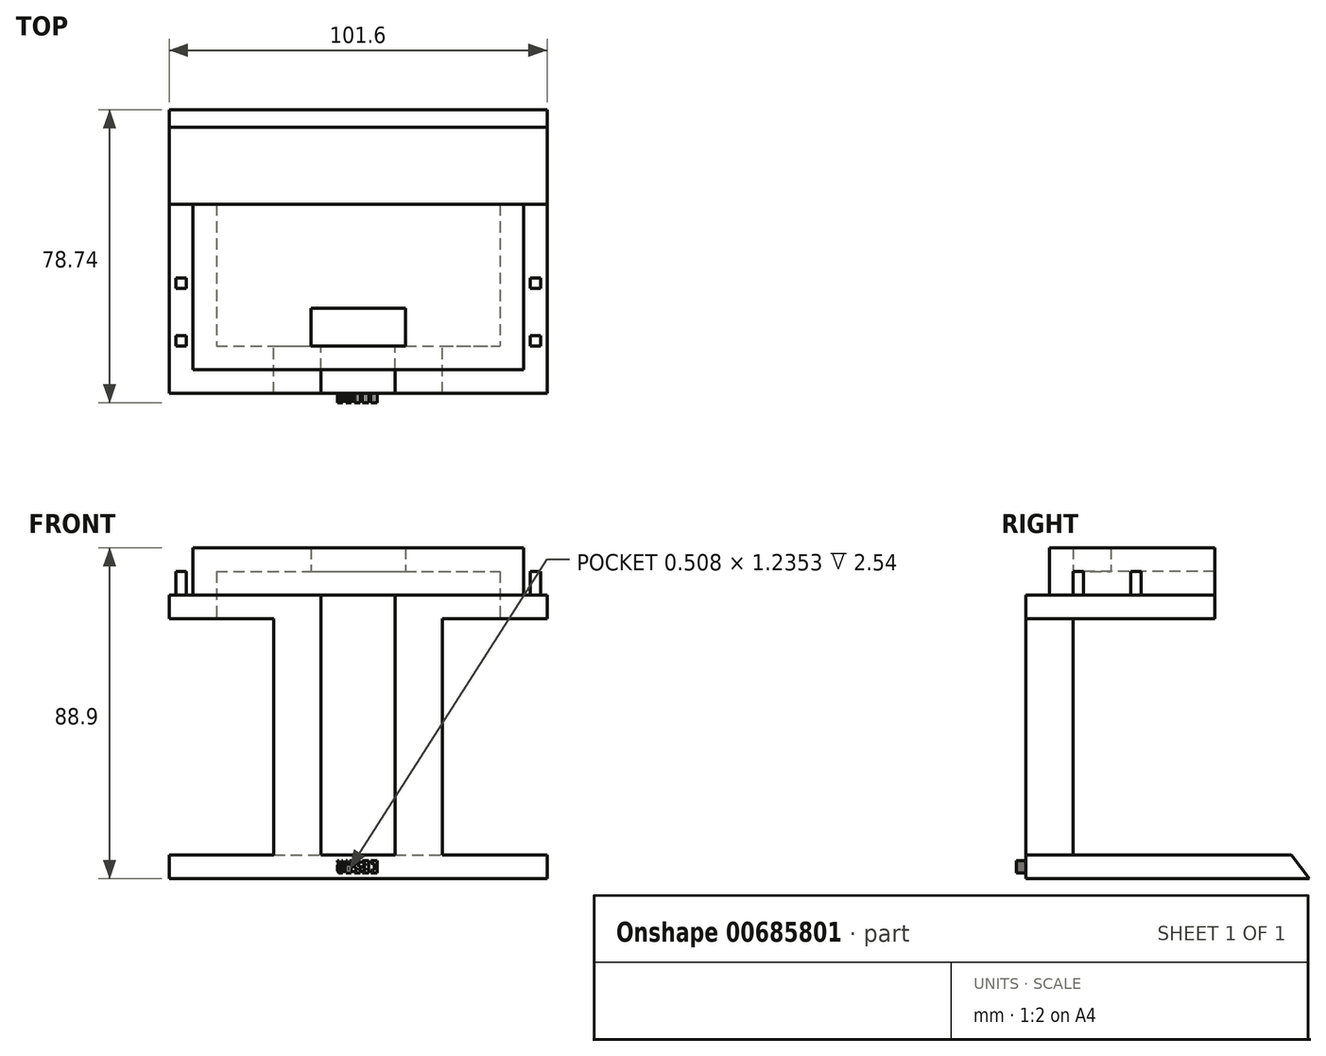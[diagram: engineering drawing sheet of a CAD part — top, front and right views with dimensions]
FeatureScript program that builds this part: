
annotation { "Feature Type Name" : "Feature", "Feature Type Description" : "" }
export const myFeature = defineFeature(function(context is Context, id is Id, definition is map)
    precondition{}
    {
        {
            var Q0;
            Q0=qCreatedBy(makeId("Top.planeOp"),FACE);
            var sketch = newSketch(context, id + "F0", { "sketchPlane" : qUnion([Q0])});
            skLineSegment(sketch, "E0.bottom", {"start": v(-43.67, 17.4) * mm, "end": v(57.93, 17.4) * mm});
            skLineSegment(sketch, "E0.top", {"start": v(-43.67, -33.4) * mm, "end": v(57.93, -33.4) * mm});
            skLineSegment(sketch, "E0.left", {"start": v(-43.67, 17.4) * mm, "end": v(-43.67, -33.4) * mm});
            skLineSegment(sketch, "E0.right", {"start": v(57.93, 17.4) * mm, "end": v(57.93, -33.4) * mm});
            skSolve(sketch);
        }
        {
            var Q0;
            Q0=makeQuery(id+"F0.imprint","IMPRINT",FACE,{"disambiguationData":[TD([[makeQuery(id+"F0.imprint","IMPRINT",EDGE,{"derivedFrom":sQuery(id+"F0.wireOp",EDGE,"E0.bottom")}),-1.0]])]});
            extrude(context, id + "F1", {"entities" : qUnion([Q0]), "depth" : 19.05 * mm, "offsetDistance" : 25.4 * mm});
        }
        {
            var Q0;
            Q0=makeQuery(id+"F1.opExtrude","CAP_FACE",FACE,{"disambiguationData":[OSD([sQuery(id+"F0.wireOp",EDGE,"E0.bottom"),sQuery(id+"F0.wireOp",EDGE,"E0.top"),sQuery(id+"F0.wireOp",EDGE,"E0.left"),sQuery(id+"F0.wireOp",EDGE,"E0.right")])],"isStart":false});
            var sketch = newSketch(context, id + "F2", { "sketchPlane" : qUnion([Q0])});
            skLineSegment(sketch, "E1.bottom", {"start": v(-37.32, 17.4) * mm, "end": v(51.58, 17.4) * mm});
            skLineSegment(sketch, "E1.top", {"start": v(-37.32, -33.4) * mm, "end": v(51.58, -33.4) * mm});
            skLineSegment(sketch, "E1.left", {"start": v(-37.32, 17.4) * mm, "end": v(-37.32, -33.4) * mm});
            skLineSegment(sketch, "E1.right", {"start": v(51.58, 17.4) * mm, "end": v(51.58, -33.4) * mm});
            skLineSegment(sketch, "E2", {"start": v(-37.32, -27.04) * mm, "end": v(51.58, -27.04) * mm});
            skSolve(sketch);
        }
        {
            var Q0;
            {var subQ0=makeQuery(id+"F1.opExtrude","CAP_EDGE",EDGE,{"disambiguationData":[OSD([sQuery(id+"F0.wireOp",EDGE,"E0.left")])],"isStart":false});Q0=makeQuery(id+"F2.imprint","IMPRINT",FACE,{"disambiguationData":[TD([[makeQuery(id+"F2.imprint","IMPRINT",EDGE,{"derivedFrom":subQ0}),1.0]])]});}
            var Q1;
            {var subQ0=sQuery(id+"F2.wireOp",EDGE,"E1.top");Q1=makeQuery(id+"F2.imprint","IMPRINT",FACE,{"disambiguationData":[TD([[makeQuery(id+"F2.imprint","IMPRINT",EDGE,{"derivedFrom":subQ0}),1.0]])]});}
            var Q2;
            {var subQ0=makeQuery(id+"F1.opExtrude","CAP_EDGE",EDGE,{"disambiguationData":[OSD([sQuery(id+"F0.wireOp",EDGE,"E0.right")])],"isStart":false});Q2=makeQuery(id+"F2.imprint","IMPRINT",FACE,{"disambiguationData":[TD([[makeQuery(id+"F2.imprint","IMPRINT",EDGE,{"derivedFrom":subQ0}),-1.0]])]});}
            extrude(context, id + "F3", {"entities" : qUnion([Q0, Q1, Q2]), "operationType" : NewBodyOperationType.REMOVE, "oppositeDirection" : true, "depth" : 12.7 * mm, "offsetDistance" : 25.4 * mm});
        }
        {
            var Q0;
            Q0=makeQuery(id+"F1.opExtrude","CAP_FACE",FACE,{"disambiguationData":[OSD([sQuery(id+"F0.wireOp",EDGE,"E0.bottom"),sQuery(id+"F0.wireOp",EDGE,"E0.top"),sQuery(id+"F0.wireOp",EDGE,"E0.left"),sQuery(id+"F0.wireOp",EDGE,"E0.right")])],"isStart":true});
            var sketch = newSketch(context, id + "F4", { "sketchPlane" : qUnion([Q0])});
            skLineSegment(sketch, "E3.bottom", {"start": v(-30.97, -17.4) * mm, "end": v(45.23, -17.4) * mm});
            skLineSegment(sketch, "E3.top", {"start": v(-30.97, 20.7) * mm, "end": v(45.23, 20.7) * mm});
            skLineSegment(sketch, "E3.left", {"start": v(-30.97, -17.4) * mm, "end": v(-30.97, 20.7) * mm});
            skLineSegment(sketch, "E3.right", {"start": v(45.23, -17.4) * mm, "end": v(45.23, 20.7) * mm});
            skSolve(sketch);
        }
        {
            var Q0;
            Q0=makeQuery(id+"F4.imprint","IMPRINT",FACE,{"disambiguationData":[TD([[makeQuery(id+"F4.imprint","IMPRINT",EDGE,{"derivedFrom":sQuery(id+"F4.wireOp",EDGE,"E3.bottom")}),1.0]])]});
            extrude(context, id + "F5", {"entities" : qUnion([Q0]), "operationType" : NewBodyOperationType.REMOVE, "oppositeDirection" : true, "depth" : 12.7 * mm, "offsetDistance" : 25.4 * mm});
        }
        {
            var Q0;
            Q0=makeQuery(id+"F5.boolean.opBoolean","COPY",FACE,{"derivedFrom":makeQuery(id+"F5.opExtrude","CAP_FACE",FACE,{"disambiguationData":[OSD([sQuery(id+"F4.wireOp",EDGE,"E3.bottom"),sQuery(id+"F4.wireOp",EDGE,"E3.top"),sQuery(id+"F4.wireOp",EDGE,"E3.left"),sQuery(id+"F4.wireOp",EDGE,"E3.right")])],"isStart":false})});
            var sketch = newSketch(context, id + "F6", { "sketchPlane" : qUnion([Q0])});
            skLineSegment(sketch, "E4.bottom", {"start": v(-5.57, 20.7) * mm, "end": v(19.83, 20.7) * mm});
            skLineSegment(sketch, "E4.top", {"start": v(-5.57, 10.53) * mm, "end": v(19.83, 10.53) * mm});
            skLineSegment(sketch, "E4.left", {"start": v(-5.57, 20.7) * mm, "end": v(-5.57, 10.53) * mm});
            skLineSegment(sketch, "E4.right", {"start": v(19.83, 20.7) * mm, "end": v(19.83, 10.53) * mm});
            skSolve(sketch);
        }
        {
            var Q0;
            Q0=makeQuery(id+"F6.imprint","IMPRINT",FACE,{"disambiguationData":[TD([[makeQuery(id+"F6.imprint","IMPRINT",EDGE,{"derivedFrom":sQuery(id+"F6.wireOp",EDGE,"E4.bottom")}),-1.0]])]});
            extrude(context, id + "F7", {"entities" : qUnion([Q0]), "operationType" : NewBodyOperationType.REMOVE, "oppositeDirection" : true, "depth" : 25.4 * mm, "offsetDistance" : 25.4 * mm});
        }
        {
            var Q0;
            Q0=makeQuery(id+"F1.opExtrude","CAP_FACE",FACE,{"disambiguationData":[OSD([sQuery(id+"F0.wireOp",EDGE,"E0.bottom"),sQuery(id+"F0.wireOp",EDGE,"E0.top"),sQuery(id+"F0.wireOp",EDGE,"E0.left"),sQuery(id+"F0.wireOp",EDGE,"E0.right")])],"isStart":true});
            var sketch = newSketch(context, id + "F8", { "sketchPlane" : qUnion([Q0])});
            skLineSegment(sketch, "E5.bottom", {"start": v(-2.83, 33.4) * mm, "end": v(17.08, 33.4) * mm});
            skLineSegment(sketch, "E5.top", {"start": v(-2.83, 20.7) * mm, "end": v(17.08, 20.7) * mm});
            skLineSegment(sketch, "E5.left", {"start": v(-2.83, 33.4) * mm, "end": v(-2.83, 20.7) * mm});
            skLineSegment(sketch, "E5.right", {"start": v(17.08, 33.4) * mm, "end": v(17.08, 20.7) * mm});
            skSolve(sketch);
        }
        {
            var Q0;
            Q0=makeQuery(id+"F8.imprint","IMPRINT",FACE,{"disambiguationData":[TD([[makeQuery(id+"F8.imprint","IMPRINT",EDGE,{"derivedFrom":sQuery(id+"F8.wireOp",EDGE,"E5.bottom")}),-1.0]])]});
            extrude(context, id + "F9", {"entities" : qUnion([Q0]), "operationType" : NewBodyOperationType.REMOVE, "oppositeDirection" : true, "depth" : 6.35 * mm, "offsetDistance" : 25.4 * mm});
        }
        {
            var Q0;
            {var subQ0=sQuery(id+"F0.wireOp",EDGE,"E0.bottom");var subQ1=sQuery(id+"F0.wireOp",EDGE,"E0.top");var subQ2=sQuery(id+"F0.wireOp",EDGE,"E0.right");Q0=makeQuery(id+"F9.boolean.opBoolean","SPLIT",FACE,{"disambiguationData":[TD([makeQuery(id+"F1.opExtrude","SWEPT_FACE",FACE,{"disambiguationData":[OSD([subQ2])]})])],"derivedFrom":makeQuery(id+"F1.opExtrude","CAP_FACE",FACE,{"disambiguationData":[OSD([subQ0,subQ1,sQuery(id+"F0.wireOp",EDGE,"E0.left"),subQ2])],"isStart":true})});}
            var sketch = newSketch(context, id + "F10", { "sketchPlane" : qUnion([Q0])});
            skLineSegment(sketch, "E6.bottom", {"start": v(29.78, 33.4) * mm, "end": v(17.08, 33.4) * mm});
            skLineSegment(sketch, "E6.top", {"start": v(29.78, 20.7) * mm, "end": v(17.08, 20.7) * mm});
            skLineSegment(sketch, "E6.left", {"start": v(29.78, 33.4) * mm, "end": v(29.78, 20.7) * mm});
            skLineSegment(sketch, "E6.right", {"start": v(17.08, 33.4) * mm, "end": v(17.08, 20.7) * mm});
            skLineSegment(sketch, "E7.bottom", {"start": v(-15.53, 33.4) * mm, "end": v(-2.83, 33.4) * mm});
            skLineSegment(sketch, "E7.top", {"start": v(-15.53, 20.7) * mm, "end": v(-2.83, 20.7) * mm});
            skLineSegment(sketch, "E7.left", {"start": v(-15.53, 33.4) * mm, "end": v(-15.53, 20.7) * mm});
            skLineSegment(sketch, "E7.right", {"start": v(-2.83, 33.4) * mm, "end": v(-2.83, 20.7) * mm});
            skSolve(sketch);
        }
        {
            var Q0;
            Q0=makeQuery(id+"F10.imprint","IMPRINT",FACE,{"disambiguationData":[TD([[makeQuery(id+"F10.imprint","IMPRINT",EDGE,{"derivedFrom":sQuery(id+"F10.wireOp",EDGE,"E6.bottom")}),-1.0]])]});
            var Q1;
            Q1=makeQuery(id+"F10.imprint","IMPRINT",FACE,{"disambiguationData":[TD([[makeQuery(id+"F10.imprint","IMPRINT",EDGE,{"derivedFrom":sQuery(id+"F10.wireOp",EDGE,"E7.bottom")}),-1.0]])]});
            extrude(context, id + "F11", {"entities" : qUnion([Q0, Q1]), "operationType" : NewBodyOperationType.ADD, "depth" : 63.5 * mm, "offsetDistance" : 25.4 * mm});
        }
        {
            var Q0;
            Q0=makeQuery(id+"F11.opExtrude","CAP_FACE",FACE,{"disambiguationData":[OSD([sQuery(id+"F10.wireOp",EDGE,"E7.bottom"),sQuery(id+"F10.wireOp",EDGE,"E7.top"),sQuery(id+"F10.wireOp",EDGE,"E7.left"),sQuery(id+"F10.wireOp",EDGE,"E7.right")])],"isStart":false});
            var sketch = newSketch(context, id + "F12", { "sketchPlane" : qUnion([Q0])});
            skLineSegment(sketch, "E8.bottom", {"start": v(-43.67, -42.8) * mm, "end": v(57.93, -42.8) * mm});
            skLineSegment(sketch, "E8.top", {"start": v(-43.67, 33.4) * mm, "end": v(57.93, 33.4) * mm});
            skLineSegment(sketch, "E8.left", {"start": v(-43.67, -42.8) * mm, "end": v(-43.67, 33.4) * mm});
            skLineSegment(sketch, "E8.right", {"start": v(57.93, -42.8) * mm, "end": v(57.93, 33.4) * mm});
            skSolve(sketch);
        }
        {
            var Q0;
            Q0=makeQuery(id+"F12.imprint","IMPRINT",FACE,{"disambiguationData":[TD([[makeQuery(id+"F12.imprint","IMPRINT",EDGE,{"derivedFrom":sQuery(id+"F12.wireOp",EDGE,"E8.bottom")}),1.0]])]});
            var Q1;
            Q1=makeQuery(id+"F12.imprint","IMPRINT",FACE,{"disambiguationData":[TD([[makeQuery(id+"F12.imprint","IMPRINT",EDGE,{"derivedFrom":makeQuery(id+"F11.opExtrude","CAP_EDGE",EDGE,{"disambiguationData":[OSD([sQuery(id+"F10.wireOp",EDGE,"E7.top")])],"isStart":false})}),1.0]])]});
            extrude(context, id + "F13", {"entities" : qUnion([Q0, Q1]), "operationType" : NewBodyOperationType.ADD, "depth" : 6.35 * mm, "offsetDistance" : 25.4 * mm});
        }
        {
            var Q0;
            Q0=makeQuery(id+"F13.opExtrude","SWEPT_FACE",FACE,{"disambiguationData":[OSD([sQuery(id+"F12.wireOp",EDGE,"E8.right")])]});
            var sketch = newSketch(context, id + "F14", { "sketchPlane" : qUnion([Q0])});
            skLineSegment(sketch, "E9", {"start": v(42.8, -69.85) * mm, "end": v(38.05, -63.5) * mm});
            skSolve(sketch);
        }
        {
            var Q0;
            {var subQ0=sQuery(id+"F14.wireOp",EDGE,"E9");Q0=makeQuery(id+"F14.imprint","IMPRINT",FACE,{"disambiguationData":[TD([[makeQuery(id+"F14.imprint","IMPRINT",EDGE,{"derivedFrom":subQ0}),-1.0]])]});}
            extrude(context, id + "F15", {"entities" : qUnion([Q0]), "operationType" : NewBodyOperationType.REMOVE, "oppositeDirection" : true, "depth" : 101.6 * mm, "offsetDistance" : 25.4 * mm});
        }
        {
            var Q0;
            {var subQ0=sQuery(id+"F0.wireOp",EDGE,"E0.left");var subQ1=sQuery(id+"F0.wireOp",EDGE,"E0.top");var subQ2=sQuery(id+"F2.wireOp",EDGE,"E1.left");var subQ3=sQuery(id+"F0.wireOp",EDGE,"E0.bottom");var subQ4=sQuery(id+"F2.wireOp",EDGE,"E2");Q0=makeQuery(id+"F9.boolean.opBoolean","SPLIT",FACE,{"disambiguationData":[TD([makeQuery(id+"F1.opExtrude","SWEPT_FACE",FACE,{"disambiguationData":[OSD([subQ0])]})])],"derivedFrom":makeQuery(id+"F3.boolean.opBoolean","COPY",FACE,{"derivedFrom":makeQuery(id+"F3.opExtrude","CAP_FACE",FACE,{"disambiguationData":[OSD([subQ3,subQ1,subQ0,sQuery(id+"F0.wireOp",EDGE,"E0.right"),sQuery(id+"F2.wireOp",EDGE,"E1.top"),subQ2,sQuery(id+"F2.wireOp",EDGE,"E1.right"),subQ4])],"isStart":false})})});}
            var sketch = newSketch(context, id + "F16", { "sketchPlane" : qUnion([Q0])});
            skLineSegment(sketch, "E10.bottom", {"start": v(-41.9, -2.4) * mm, "end": v(-39.1, -2.4) * mm});
            skLineSegment(sketch, "E10.top", {"start": v(-41.9, -5.2) * mm, "end": v(-39.1, -5.2) * mm});
            skLineSegment(sketch, "E10.left", {"start": v(-41.9, -2.4) * mm, "end": v(-41.9, -5.2) * mm});
            skLineSegment(sketch, "E10.right", {"start": v(-39.1, -2.4) * mm, "end": v(-39.1, -5.2) * mm});
            skLineSegment(sketch, "E11.bottom", {"start": v(-41.9, -17.9) * mm, "end": v(-39.1, -17.9) * mm});
            skLineSegment(sketch, "E11.top", {"start": v(-41.9, -20.7) * mm, "end": v(-39.1, -20.7) * mm});
            skLineSegment(sketch, "E11.left", {"start": v(-41.9, -17.9) * mm, "end": v(-41.9, -20.7) * mm});
            skLineSegment(sketch, "E11.right", {"start": v(-39.1, -17.9) * mm, "end": v(-39.1, -20.7) * mm});
            skLineSegment(sketch, "E12.bottom", {"start": v(53.35, -17.9) * mm, "end": v(56.15, -17.9) * mm});
            skLineSegment(sketch, "E12.top", {"start": v(53.35, -20.7) * mm, "end": v(56.15, -20.7) * mm});
            skLineSegment(sketch, "E12.left", {"start": v(53.35, -17.9) * mm, "end": v(53.35, -20.7) * mm});
            skLineSegment(sketch, "E12.right", {"start": v(56.15, -17.9) * mm, "end": v(56.15, -20.7) * mm});
            skLineSegment(sketch, "E13.bottom", {"start": v(53.35, -2.4) * mm, "end": v(56.15, -2.4) * mm});
            skLineSegment(sketch, "E13.top", {"start": v(53.35, -5.2) * mm, "end": v(56.15, -5.2) * mm});
            skLineSegment(sketch, "E13.left", {"start": v(53.35, -2.4) * mm, "end": v(53.35, -5.2) * mm});
            skLineSegment(sketch, "E13.right", {"start": v(56.15, -2.4) * mm, "end": v(56.15, -5.2) * mm});
            skSolve(sketch);
        }
        {
            var Q0;
            Q0=makeQuery(id+"F16.imprint","IMPRINT",FACE,{"disambiguationData":[TD([[makeQuery(id+"F16.imprint","IMPRINT",EDGE,{"derivedFrom":sQuery(id+"F16.wireOp",EDGE,"E10.bottom")}),-1.0]])]});
            var Q1;
            Q1=makeQuery(id+"F16.imprint","IMPRINT",FACE,{"disambiguationData":[TD([[makeQuery(id+"F16.imprint","IMPRINT",EDGE,{"derivedFrom":sQuery(id+"F16.wireOp",EDGE,"E11.bottom")}),-1.0]])]});
            var Q2;
            Q2=makeQuery(id+"F16.imprint","IMPRINT",FACE,{"disambiguationData":[TD([[makeQuery(id+"F16.imprint","IMPRINT",EDGE,{"derivedFrom":sQuery(id+"F16.wireOp",EDGE,"E13.bottom")}),-1.0]])]});
            var Q3;
            Q3=makeQuery(id+"F16.imprint","IMPRINT",FACE,{"disambiguationData":[TD([[makeQuery(id+"F16.imprint","IMPRINT",EDGE,{"derivedFrom":sQuery(id+"F16.wireOp",EDGE,"E12.bottom")}),-1.0]])]});
            extrude(context, id + "F17", {"entities" : qUnion([Q0, Q1, Q2, Q3]), "operationType" : NewBodyOperationType.ADD, "depth" : 6.35 * mm, "offsetDistance" : 25.4 * mm});
        }
        {
            var Q0;
            {var subQ0=sQuery(id+"F0.wireOp",EDGE,"E0.right");var subQ1=sQuery(id+"F0.wireOp",EDGE,"E0.left");var subQ2=sQuery(id+"F0.wireOp",EDGE,"E0.top");var subQ6=makeQuery(id+"F1.opExtrude","SWEPT_FACE",FACE,{"disambiguationData":[OSD([subQ2])]});Q0=makeQuery(id+"F13.boolean.opBoolean","MERGE",FACE,{"derivedFrom":[makeQuery(id+"F11.boolean.opBoolean","MERGE",FACE,{"derivedFrom":[makeQuery(id+"F9.boolean.opBoolean","SPLIT",FACE,{"disambiguationData":[TD([makeQuery(id+"F1.opExtrude","SWEPT_FACE",FACE,{"disambiguationData":[OSD([subQ1])]})])],"derivedFrom":subQ6}),makeQuery(id+"F11.opExtrude","SWEPT_FACE",FACE,{"disambiguationData":[OSD([sQuery(id+"F10.wireOp",EDGE,"E7.bottom")])]})]}),makeQuery(id+"F11.boolean.opBoolean","MERGE",FACE,{"derivedFrom":[makeQuery(id+"F9.boolean.opBoolean","SPLIT",FACE,{"disambiguationData":[TD([makeQuery(id+"F1.opExtrude","SWEPT_FACE",FACE,{"disambiguationData":[OSD([subQ0])]})])],"derivedFrom":subQ6}),makeQuery(id+"F11.opExtrude","SWEPT_FACE",FACE,{"disambiguationData":[OSD([sQuery(id+"F10.wireOp",EDGE,"E6.bottom")])]})]}),makeQuery(id+"F13.opExtrude","SWEPT_FACE",FACE,{"disambiguationData":[OSD([sQuery(id+"F12.wireOp",EDGE,"E8.top")])]})]});}
            var sketch = newSketch(context, id + "F18", { "sketchPlane" : qUnion([Q0])});
            skLineSegment(sketch, "E14", {"start": v(10.68, -68.33) * mm, "end": v(12.2, -68.33) * mm});
            skLineSegment(sketch, "E15", {"start": v(12.2, -68.33) * mm, "end": v(12.2, -65.02) * mm});
            skLineSegment(sketch, "E16", {"start": v(12.2, -65.02) * mm, "end": v(10.68, -65.02) * mm});
            skLineSegment(sketch, "E17", {"start": v(10.68, -65.02) * mm, "end": v(10.68, -65.79) * mm});
            skLineSegment(sketch, "E18", {"start": v(10.68, -65.79) * mm, "end": v(11.44, -65.79) * mm});
            skLineSegment(sketch, "E19", {"start": v(11.44, -65.79) * mm, "end": v(11.44, -67.56) * mm});
            skLineSegment(sketch, "E20", {"start": v(11.44, -67.56) * mm, "end": v(10.68, -67.56) * mm});
            skLineSegment(sketch, "E21", {"start": v(10.68, -67.56) * mm, "end": v(10.68, -68.33) * mm});
            skLineSegment(sketch, "E22", {"start": v(9.92, -68.33) * mm, "end": v(9.92, -65.02) * mm});
            skLineSegment(sketch, "E23", {"start": v(9.92, -65.02) * mm, "end": v(8.4, -65.02) * mm});
            skLineSegment(sketch, "E24", {"start": v(8.4, -65.02) * mm, "end": v(8.4, -65.79) * mm});
            skLineSegment(sketch, "E25", {"start": v(8.4, -65.79) * mm, "end": v(9.16, -65.79) * mm});
            skLineSegment(sketch, "E26", {"start": v(9.16, -65.79) * mm, "end": v(9.16, -66.3) * mm});
            skLineSegment(sketch, "E27", {"start": v(9.16, -66.3) * mm, "end": v(8.65, -66.3) * mm});
            skLineSegment(sketch, "E28", {"start": v(8.65, -66.3) * mm, "end": v(8.65, -67.06) * mm});
            skLineSegment(sketch, "E29", {"start": v(8.65, -67.06) * mm, "end": v(9.16, -67.06) * mm});
            skLineSegment(sketch, "E30", {"start": v(9.16, -67.06) * mm, "end": v(9.16, -67.56) * mm});
            skLineSegment(sketch, "E31", {"start": v(9.16, -67.56) * mm, "end": v(8.4, -67.56) * mm});
            skLineSegment(sketch, "E32", {"start": v(8.4, -67.56) * mm, "end": v(8.4, -68.33) * mm});
            skLineSegment(sketch, "E33", {"start": v(8.4, -68.33) * mm, "end": v(9.92, -68.33) * mm});
            skLineSegment(sketch, "E34", {"start": v(6.1, -68.3) * mm, "end": v(7.63, -68.3) * mm});
            skLineSegment(sketch, "E35", {"start": v(7.63, -68.3) * mm, "end": v(7.63, -66.3) * mm});
            skLineSegment(sketch, "E36", {"start": v(7.63, -66.3) * mm, "end": v(6.87, -66.3) * mm});
            skLineSegment(sketch, "E37", {"start": v(6.87, -66.3) * mm, "end": v(6.87, -65.79) * mm});
            skLineSegment(sketch, "E38", {"start": v(6.87, -65.79) * mm, "end": v(7.63, -65.79) * mm});
            skLineSegment(sketch, "E39", {"start": v(7.63, -65.79) * mm, "end": v(7.63, -65.02) * mm});
            skLineSegment(sketch, "E40", {"start": v(7.63, -65.02) * mm, "end": v(6.1, -65.02) * mm});
            skLineSegment(sketch, "E41", {"start": v(6.1, -65.02) * mm, "end": v(6.1, -67.02) * mm});
            skLineSegment(sketch, "E42", {"start": v(6.1, -67.02) * mm, "end": v(6.87, -67.02) * mm});
            skLineSegment(sketch, "E43", {"start": v(6.87, -67.02) * mm, "end": v(6.87, -67.53) * mm});
            skLineSegment(sketch, "E44", {"start": v(6.87, -67.53) * mm, "end": v(6.1, -67.53) * mm});
            skLineSegment(sketch, "E45", {"start": v(6.1, -67.53) * mm, "end": v(6.1, -68.3) * mm});
            skLineSegment(sketch, "E46", {"start": v(5.35, -68.3) * mm, "end": v(5.35, -65.02) * mm});
            skLineSegment(sketch, "E47", {"start": v(5.35, -65.02) * mm, "end": v(4.84, -65.02) * mm});
            skLineSegment(sketch, "E48", {"start": v(4.84, -65.02) * mm, "end": v(4.84, -66.04) * mm});
            skLineSegment(sketch, "E49", {"start": v(4.84, -66.04) * mm, "end": v(4.33, -66.04) * mm});
            skLineSegment(sketch, "E50", {"start": v(4.33, -66.04) * mm, "end": v(4.33, -65.02) * mm});
            skLineSegment(sketch, "E51", {"start": v(4.33, -65.02) * mm, "end": v(3.82, -65.02) * mm});
            skLineSegment(sketch, "E52", {"start": v(3.82, -65.02) * mm, "end": v(3.82, -68.3) * mm});
            skLineSegment(sketch, "E53", {"start": v(3.82, -68.3) * mm, "end": v(5.35, -68.3) * mm});
            skLineSegment(sketch, "E54", {"start": v(4.84, -67.78) * mm, "end": v(4.84, -66.55) * mm});
            skLineSegment(sketch, "E55", {"start": v(4.84, -66.55) * mm, "end": v(4.33, -66.55) * mm});
            skLineSegment(sketch, "E56", {"start": v(4.33, -66.55) * mm, "end": v(4.33, -67.78) * mm});
            skLineSegment(sketch, "E57", {"start": v(4.33, -67.78) * mm, "end": v(4.84, -67.78) * mm});
            skLineSegment(sketch, "E58", {"start": v(3.06, -68.3) * mm, "end": v(3.06, -65.02) * mm});
            skLineSegment(sketch, "E59", {"start": v(3.06, -68.3) * mm, "end": v(1.54, -68.3) * mm});
            skLineSegment(sketch, "E60", {"start": v(1.54, -68.3) * mm, "end": v(1.54, -65.02) * mm});
            skLineSegment(sketch, "E61", {"start": v(2.68, -65.02) * mm, "end": v(2.68, -65.79) * mm});
            skLineSegment(sketch, "E62", {"start": v(2.68, -65.79) * mm, "end": v(2.3, -65.79) * mm});
            skLineSegment(sketch, "E63", {"start": v(2.3, -65.79) * mm, "end": v(1.92, -65.42) * mm});
            skLineSegment(sketch, "E64", {"start": v(1.92, -65.42) * mm, "end": v(1.92, -65.02) * mm});
            skLineSegment(sketch, "E65", {"start": v(3.06, -65.02) * mm, "end": v(2.68, -65.02) * mm});
            skLineSegment(sketch, "E66", {"start": v(1.92, -65.02) * mm, "end": v(1.54, -65.02) * mm});
            skPoint(sketch, "E67.endSnap0", {"position": v(1.73, -65.02) * mm});
            skLineSegment(sketch, "E68", {"start": v(1.54, -65.42) * mm, "end": v(1.92, -65.79) * mm});
            skLineSegment(sketch, "E69", {"start": v(1.92, -65.79) * mm, "end": v(1.54, -66.19) * mm});
            skPoint(sketch, "E70.endSnap0", {"position": v(1.73, -65.6) * mm});
            skLineSegment(sketch, "E71", {"start": v(1.92, -68.3) * mm, "end": v(1.54, -67.82) * mm});
            skLineSegment(sketch, "E72", {"start": v(1.92, -68.3) * mm, "end": v(2.3, -68.3) * mm});
            skLineSegment(sketch, "E73", {"start": v(2.68, -66.19) * mm, "end": v(2.68, -67.82) * mm});
            skLineSegment(sketch, "E74", {"start": v(2.68, -67.82) * mm, "end": v(2.1, -67.82) * mm});
            skPoint(sketch, "E74.endSnap0", {"position": v(2.1, -68.3) * mm});
            skLineSegment(sketch, "E75", {"start": v(2.68, -66.19) * mm, "end": v(2.1, -66.19) * mm});
            skLineSegment(sketch, "E76", {"start": v(2.1, -66.19) * mm, "end": v(1.92, -66.39) * mm});
            skLineSegment(sketch, "E77", {"start": v(2.1, -67.82) * mm, "end": v(1.92, -67.64) * mm});
            skLineSegment(sketch, "E78", {"start": v(1.92, -67.64) * mm, "end": v(1.92, -66.39) * mm});
            skSolve(sketch);
        }
        {
            var Q0;
            Q0=makeQuery(id+"F18.imprint","IMPRINT",FACE,{"disambiguationData":[TD([[makeQuery(id+"F18.imprint","IMPRINT",EDGE,{"derivedFrom":sQuery(id+"F18.wireOp",EDGE,"E14")}),1.0]])]});
            var Q1;
            Q1=makeQuery(id+"F18.imprint","IMPRINT",FACE,{"disambiguationData":[TD([[makeQuery(id+"F18.imprint","IMPRINT",EDGE,{"derivedFrom":sQuery(id+"F18.wireOp",EDGE,"E22")}),1.0]])]});
            var Q2;
            Q2=makeQuery(id+"F18.imprint","IMPRINT",FACE,{"disambiguationData":[TD([[makeQuery(id+"F18.imprint","IMPRINT",EDGE,{"derivedFrom":sQuery(id+"F18.wireOp",EDGE,"E34")}),1.0]])]});
            var Q3;
            Q3=makeQuery(id+"F18.imprint","IMPRINT",FACE,{"disambiguationData":[TD([[makeQuery(id+"F18.imprint","IMPRINT",EDGE,{"derivedFrom":sQuery(id+"F18.wireOp",EDGE,"E46")}),1.0]])]});
            var Q4;
            {var subQ0=sQuery(id+"F18.wireOp",EDGE,"E58");Q4=makeQuery(id+"F18.imprint","IMPRINT",FACE,{"disambiguationData":[TD([[makeQuery(id+"F18.imprint","IMPRINT",EDGE,{"derivedFrom":subQ0}),1.0]])]});}
            extrude(context, id + "F19", {"entities" : qUnion([Q0, Q1, Q2, Q3, Q4]), "operationType" : NewBodyOperationType.ADD, "depth" : 2.54 * mm, "offsetDistance" : 25.4 * mm});
        }
    });
